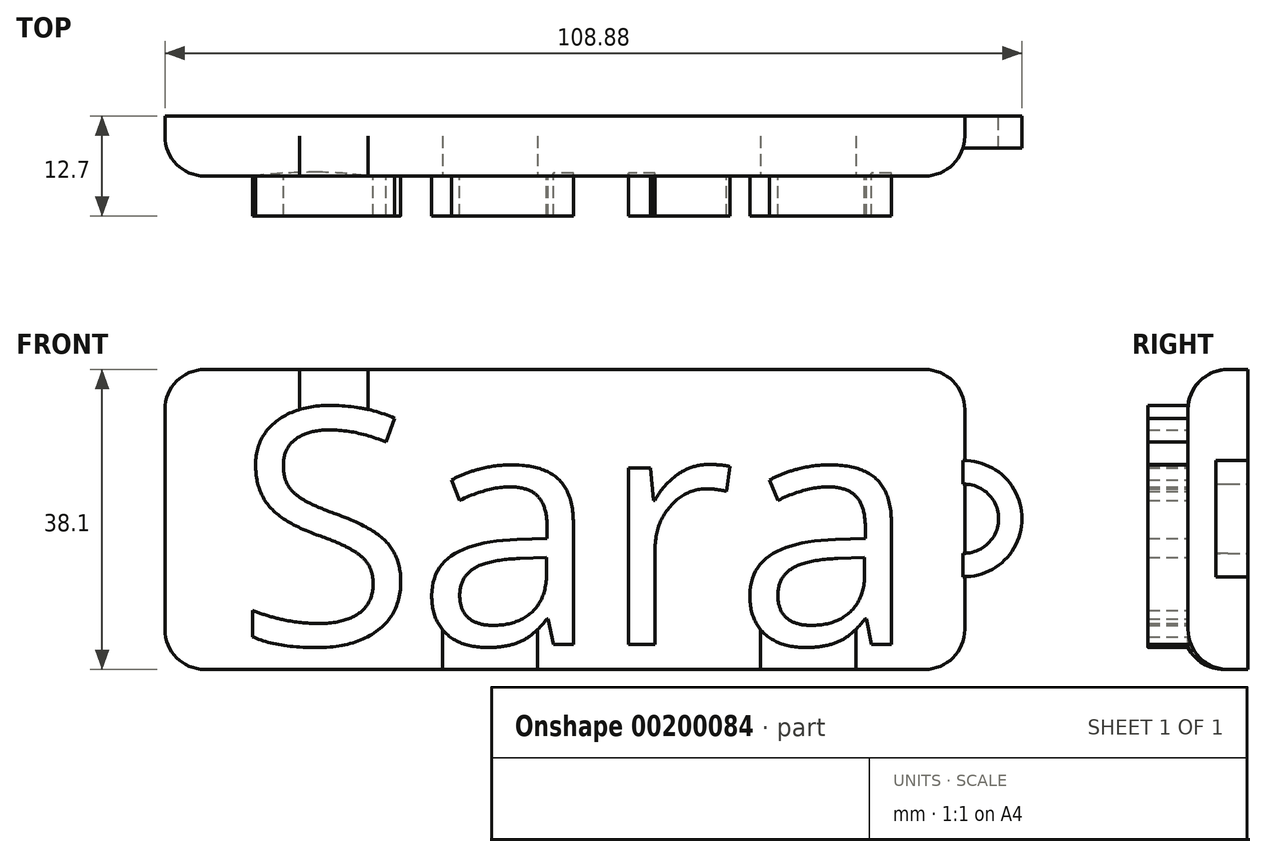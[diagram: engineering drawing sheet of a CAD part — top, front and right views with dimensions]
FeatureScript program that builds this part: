
annotation { "Feature Type Name" : "Feature", "Feature Type Description" : "" }
export const myFeature = defineFeature(function(context is Context, id is Id, definition is map)
    precondition{}
    {
        {
            var Q0;
            Q0=qCreatedBy(makeId("Front.planeOp"),FACE);
            var sketch = newSketch(context, id + "F0", { "sketchPlane" : qUnion([Q0])});
            skLineSegment(sketch, "E0.bottom", {"start": v(-76.8, 37.06) * mm, "end": v(24.8, 37.06) * mm});
            skLineSegment(sketch, "E0.top", {"start": v(-76.8, -1.04) * mm, "end": v(24.8, -1.04) * mm});
            skLineSegment(sketch, "E0.left", {"start": v(-76.8, 37.06) * mm, "end": v(-76.8, -1.04) * mm});
            skLineSegment(sketch, "E0.right", {"start": v(24.8, 37.06) * mm, "end": v(24.8, -1.04) * mm});
            skSolve(sketch);
        }
        {
            var Q0;
            Q0=makeQuery(id+"F0.imprint","IMPRINT",FACE,{"disambiguationData":[TD([[makeQuery(id+"F0.imprint","IMPRINT",EDGE,{"derivedFrom":sQuery(id+"F0.wireOp",EDGE,"E0.bottom")}),-1.0]])]});
            extrude(context, id + "F1", {"entities" : qUnion([Q0]), "depth" : 7.62 * mm});
        }
        {
            var Q0;
            Q0=makeQuery(id+"F1.opExtrude","CAP_FACE",FACE,{"disambiguationData":[OSD([sQuery(id+"F0.wireOp",EDGE,"E0.bottom"),sQuery(id+"F0.wireOp",EDGE,"E0.top"),sQuery(id+"F0.wireOp",EDGE,"E0.left"),sQuery(id+"F0.wireOp",EDGE,"E0.right")])],"isStart":false});
            var sketch = newSketch(context, id + "F2", { "sketchPlane" : qUnion([Q0])});
            skText(sketch, "E1", { "text": "Sara", "fontName": "OpenSans-Regular.ttf"});
            const initialGuessF2  = {"E1": [-0.06783, 0.00216, 1, 0, 0.03017]};
            skSetInitialGuess(sketch, initialGuessF2);
            skSolve(sketch);
        }
        {
            var Q0;
            Q0 = qSketchRegion(id + "F2", true);
            extrude(context, id + "F3", {"entities" : qUnion([Q0]), "operationType" : NewBodyOperationType.ADD, "depth" : 5.08 * mm});
        }
        {
            var Q0;
            Q0=makeQuery(id+"F1.opExtrude","CAP_EDGE",EDGE,{"disambiguationData":[OSD([sQuery(id+"F0.wireOp",EDGE,"E0.left")])],"isStart":false});
            fillet(context, id + "F4", {"entities" : qUnion([Q0]), "radius" : 5.08 * mm, "tangentPropagation" : true, "allowEdgeOverflow" : false});
        }
        {
            var Q0;
            Q0=makeQuery(id+"F1.opExtrude","CAP_EDGE",EDGE,{"disambiguationData":[OSD([sQuery(id+"F0.wireOp",EDGE,"E0.right")])],"isStart":false});
            fillet(context, id + "F5", {"entities" : qUnion([Q0]), "radius" : 5.08 * mm, "tangentPropagation" : true, "allowEdgeOverflow" : false});
        }
        {
            var Q0;
            Q0=makeQuery(id+"F1.opExtrude","CAP_EDGE",EDGE,{"disambiguationData":[OSD([sQuery(id+"F0.wireOp",EDGE,"E0.bottom")])],"isStart":false});
            fillet(context, id + "F6", {"entities" : qUnion([Q0]), "radius" : 5.08 * mm, "tangentPropagation" : true, "allowEdgeOverflow" : false});
        }
        {
            var Q0;
            Q0=makeQuery(id+"F1.opExtrude","CAP_EDGE",EDGE,{"disambiguationData":[OSD([sQuery(id+"F0.wireOp",EDGE,"E0.top")])],"isStart":false});
            fillet(context, id + "F7", {"entities" : qUnion([Q0]), "radius" : 5.08 * mm, "tangentPropagation" : true, "allowEdgeOverflow" : false});
        }
        {
            var Q0;
            Q0=qCreatedBy(makeId("Front.planeOp"),FACE);
            var sketch = newSketch(context, id + "F8", { "sketchPlane" : qUnion([Q0])});
            skCircle(sketch, "E2", {"center": v(24.72, 18.12) * mm, "radius": 7.37 * mm});
            skCircle(sketch, "E3", {"center": v(24.72, 18.12) * mm, "radius": 4.4 * mm});
            skSolve(sketch);
        }
        {
            var Q0;
            Q0 = qSketchRegion(id + "F8", true);
            extrude(context, id + "F9", {"entities" : qUnion([Q0]), "operationType" : NewBodyOperationType.ADD, "depth" : 4.06 * mm});
        }
    });
